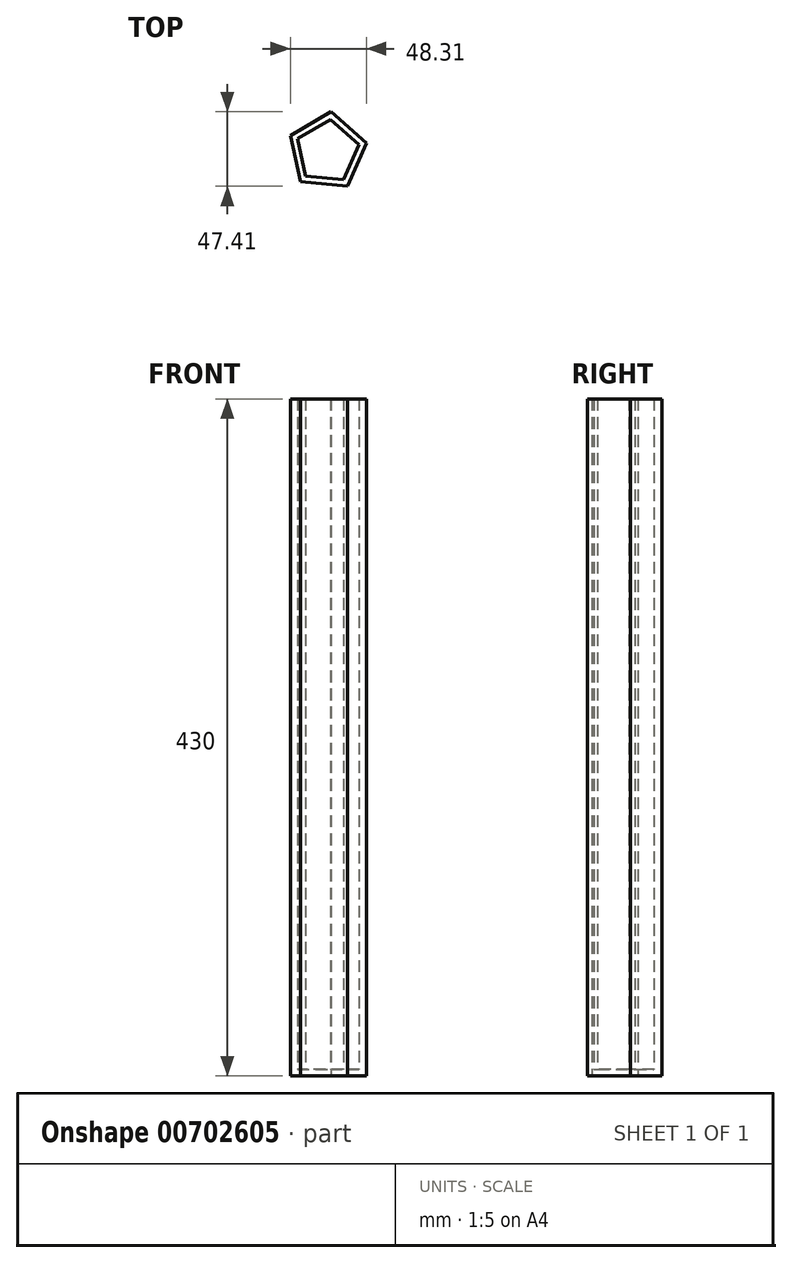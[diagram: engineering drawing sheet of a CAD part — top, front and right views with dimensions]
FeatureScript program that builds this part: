
annotation { "Feature Type Name" : "Feature", "Feature Type Description" : "" }
export const myFeature = defineFeature(function(context is Context, id is Id, definition is map)
    precondition{}
    {
        {
            var Q0;
            Q0=qCreatedBy(makeId("Top.planeOp"),FACE);
            var sketch = newSketch(context, id + "F0", { "sketchPlane" : qUnion([Q0])});
            skCircle(sketch, "E0.cCircle", {"center": v(0, 0) * mm, "radius": 20.65 * mm, "construction": true});
            skLineSegment(sketch, "E0.0", {"start": v(-23.39, 10.21) * mm, "end": v(2.49, 25.4) * mm});
            skLineSegment(sketch, "E0.1", {"start": v(2.49, 25.4) * mm, "end": v(24.92, 5.48) * mm});
            skLineSegment(sketch, "E0.2", {"start": v(24.92, 5.48) * mm, "end": v(12.92, -22) * mm});
            skLineSegment(sketch, "E0.3", {"start": v(12.92, -22) * mm, "end": v(-16.94, -19.09) * mm});
            skLineSegment(sketch, "E0.4", {"start": v(-16.94, -19.09) * mm, "end": v(-23.39, 10.21) * mm});
            skPoint(sketch, "E0.0.midPoint", {"position": v(-10.45, 17.8) * mm});
            skSolve(sketch);
        }
        {
            var Q0;
            Q0 = qSketchRegion(id + "F0", true);
            extrude(context, id + "F1", {"entities" : qUnion([Q0]), "depth" : 430 * mm, "offsetDistance" : 25.4 * mm});
        }
        {
            var Q0;
            Q0=makeQuery(id+"F1.opExtrude","CAP_FACE",FACE,{"disambiguationData":[OSD([sQuery(id+"F0.wireOp",EDGE,"E0.0"),sQuery(id+"F0.wireOp",EDGE,"E0.1"),sQuery(id+"F0.wireOp",EDGE,"E0.2"),sQuery(id+"F0.wireOp",EDGE,"E0.3"),sQuery(id+"F0.wireOp",EDGE,"E0.4")])],"isStart":false});
            shell(context, id + "F2", {"entities" : qUnion([Q0]), "thickness" : 4 * mm});
        }
    });
